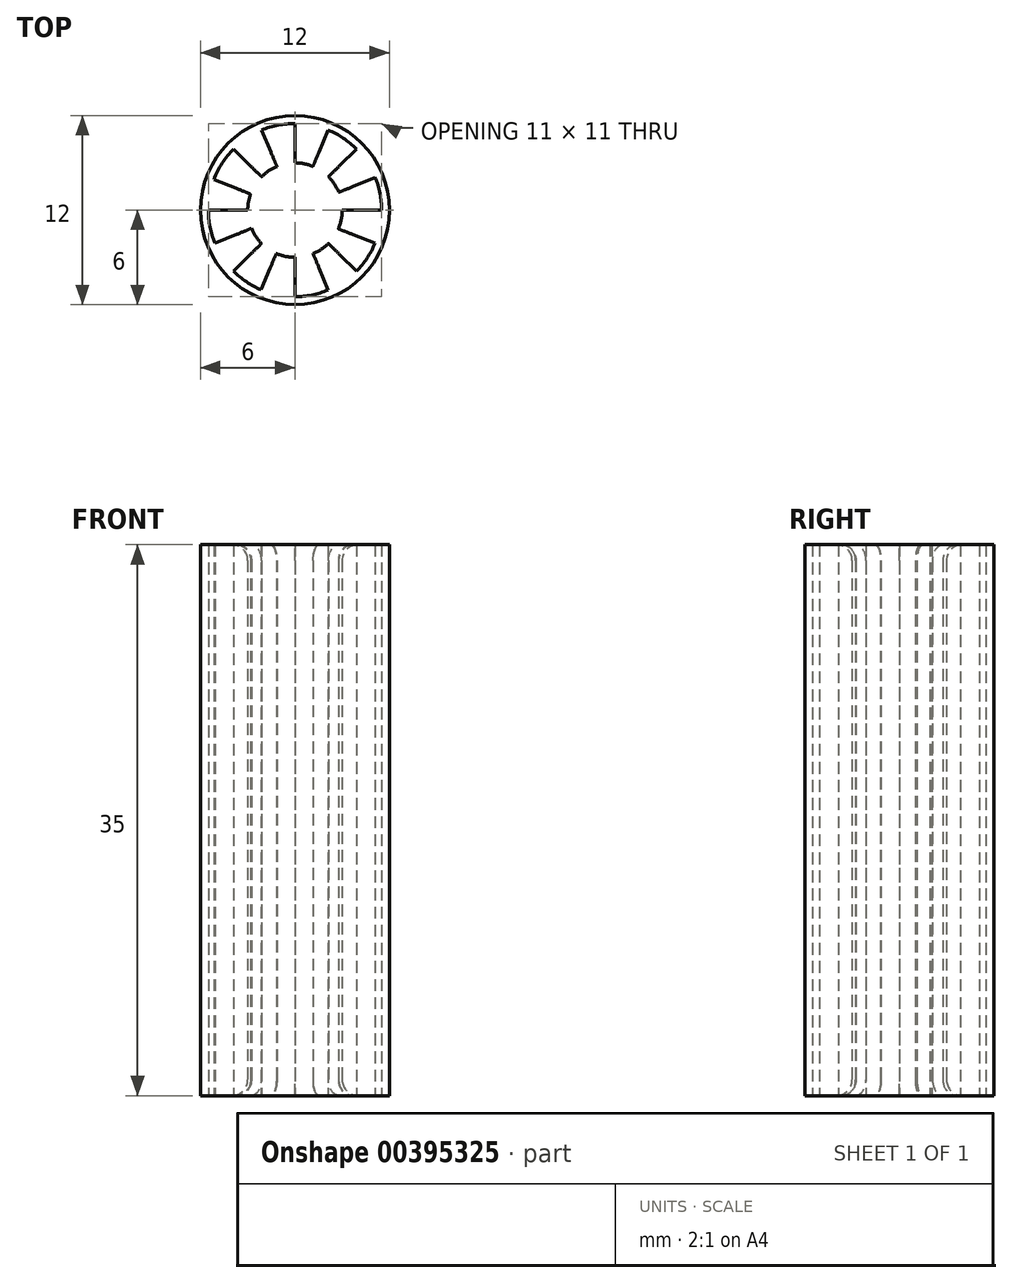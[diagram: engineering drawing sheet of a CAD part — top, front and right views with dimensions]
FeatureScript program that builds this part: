
annotation { "Feature Type Name" : "Feature", "Feature Type Description" : "" }
export const myFeature = defineFeature(function(context is Context, id is Id, definition is map)
    precondition{}
    {
        {
            var Q0;
            Q0=qCreatedBy(makeId("Top.planeOp"),FACE);
            var sketch = newSketch(context, id + "F0", { "sketchPlane" : qUnion([Q0])});
            skCircle(sketch, "E0", {"center": v(0, 0) * mm, "radius": 6 * mm});
            skCircle(sketch, "E1", {"center": v(0, 0) * mm, "radius": 3 * mm});
            skCircle(sketch, "E2", {"center": v(0, 0) * mm, "radius": 5.5 * mm});
            skLineSegment(sketch, "E3", {"start": v(0, 5.5) * mm, "end": v(0, -5.5) * mm});
            skLineSegment(sketch, "E4", {"start": v(-5.5, 0) * mm, "end": v(5.5, 0) * mm});
            skPoint(sketch, "E5", {"position": v(-3.9, 3.88) * mm});
            skPoint(sketch, "E6", {"position": v(3.9, 3.88) * mm});
            skPoint(sketch, "E7", {"position": v(-3.9, -3.88) * mm});
            skPoint(sketch, "E8", {"position": v(3.9, -3.88) * mm});
            skLineSegment(sketch, "E9", {"start": v(-3.9, 3.88) * mm, "end": v(3.9, -3.88) * mm});
            skLineSegment(sketch, "E10", {"start": v(3.9, 3.88) * mm, "end": v(-3.9, -3.88) * mm});
            skPoint(sketch, "E11", {"position": v(-2.1, 5.08) * mm});
            skPoint(sketch, "E12", {"position": v(2.11, -5.08) * mm});
            skPoint(sketch, "E13", {"position": v(5.08, -2.1) * mm});
            skPoint(sketch, "E14", {"position": v(5.1, 2.08) * mm});
            skPoint(sketch, "E15", {"position": v(2.1, 5.08) * mm});
            skPoint(sketch, "E16", {"position": v(-5.15, 1.94) * mm});
            skPoint(sketch, "E17", {"position": v(-5.08, -2.1) * mm});
            skPoint(sketch, "E18", {"position": v(-2.15, -5.06) * mm});
            skLineSegment(sketch, "E19", {"start": v(-2.1, 5.08) * mm, "end": v(2.11, -5.08) * mm});
            skLineSegment(sketch, "E20", {"start": v(5.1, 2.08) * mm, "end": v(-5.08, -2.1) * mm});
            skLineSegment(sketch, "E21", {"start": v(2.11, 5.08) * mm, "end": v(-2.15, -5.06) * mm});
            skLineSegment(sketch, "E22", {"start": v(-5.15, 1.94) * mm, "end": v(5.08, -2.1) * mm});
            skSolve(sketch);
        }
        {
            var Q0;
            Q0=qSketchRegion(id+"F0",true);
            var Q1;
            {var subQ0=sQuery(id+"F0.wireOp",EDGE,"E22");var subQ1=sQuery(id+"F0.wireOp",EDGE,"E1");var subQ2=makeQuery(id+"F0.imprint","INTERSECT",VERTEX,{"disambiguationData":[OD(0.0)],"derivedFrom":[subQ1,subQ0]});Q1=makeQuery(id+"F0.imprint","IMPRINT",FACE,{"disambiguationData":[TD([[makeQuery(id+"F0.imprint","IMPRINT",EDGE,{"disambiguationData":[TD([[subQ2,-1.0]])],"derivedFrom":subQ1}),-1.0]])]});}
            var Q2;
            {var subQ0=sQuery(id+"F0.wireOp",EDGE,"E19");var subQ1=sQuery(id+"F0.wireOp",EDGE,"E1");var subQ2=makeQuery(id+"F0.imprint","INTERSECT",VERTEX,{"disambiguationData":[OD(0.0)],"derivedFrom":[subQ1,subQ0]});Q2=makeQuery(id+"F0.imprint","IMPRINT",FACE,{"disambiguationData":[TD([[makeQuery(id+"F0.imprint","IMPRINT",EDGE,{"disambiguationData":[TD([[subQ2,-1.0]])],"derivedFrom":subQ1}),-1.0]])]});}
            var Q3;
            {var subQ0=sQuery(id+"F0.wireOp",EDGE,"E21");var subQ1=sQuery(id+"F0.wireOp",EDGE,"E1");var subQ2=makeQuery(id+"F0.imprint","INTERSECT",VERTEX,{"disambiguationData":[OD(0.0)],"derivedFrom":[subQ1,subQ0]});Q3=makeQuery(id+"F0.imprint","IMPRINT",FACE,{"disambiguationData":[TD([[makeQuery(id+"F0.imprint","IMPRINT",EDGE,{"disambiguationData":[TD([[subQ2,-1.0]])],"derivedFrom":subQ1}),-1.0]])]});}
            var Q4;
            {var subQ0=sQuery(id+"F0.wireOp",EDGE,"E20");var subQ1=sQuery(id+"F0.wireOp",EDGE,"E1");var subQ2=makeQuery(id+"F0.imprint","INTERSECT",VERTEX,{"disambiguationData":[OD(0.0)],"derivedFrom":[subQ1,subQ0]});Q4=makeQuery(id+"F0.imprint","IMPRINT",FACE,{"disambiguationData":[TD([[makeQuery(id+"F0.imprint","IMPRINT",EDGE,{"disambiguationData":[TD([[subQ2,-1.0]])],"derivedFrom":subQ1}),-1.0]])]});}
            var Q5;
            {var subQ0=sQuery(id+"F0.wireOp",EDGE,"E4");var subQ1=sQuery(id+"F0.wireOp",EDGE,"E1");var subQ2=makeQuery(id+"F0.imprint","INTERSECT",VERTEX,{"disambiguationData":[OD(0.0)],"derivedFrom":[subQ1,subQ0]});Q5=makeQuery(id+"F0.imprint","IMPRINT",FACE,{"disambiguationData":[TD([[makeQuery(id+"F0.imprint","IMPRINT",EDGE,{"disambiguationData":[TD([[subQ2,1.0]])],"derivedFrom":subQ1}),-1.0]])]});}
            var Q6;
            {var subQ0=sQuery(id+"F0.wireOp",EDGE,"E19");var subQ1=sQuery(id+"F0.wireOp",EDGE,"E1");var subQ2=makeQuery(id+"F0.imprint","INTERSECT",VERTEX,{"disambiguationData":[OD(1.0)],"derivedFrom":[subQ1,subQ0]});Q6=makeQuery(id+"F0.imprint","IMPRINT",FACE,{"disambiguationData":[TD([[makeQuery(id+"F0.imprint","IMPRINT",EDGE,{"disambiguationData":[TD([[subQ2,-1.0]])],"derivedFrom":subQ1}),-1.0]])]});}
            var Q7;
            {var subQ0=sQuery(id+"F0.wireOp",EDGE,"E21");var subQ1=sQuery(id+"F0.wireOp",EDGE,"E1");var subQ2=makeQuery(id+"F0.imprint","INTERSECT",VERTEX,{"disambiguationData":[OD(1.0)],"derivedFrom":[subQ1,subQ0]});Q7=makeQuery(id+"F0.imprint","IMPRINT",FACE,{"disambiguationData":[TD([[makeQuery(id+"F0.imprint","IMPRINT",EDGE,{"disambiguationData":[TD([[subQ2,-1.0]])],"derivedFrom":subQ1}),-1.0]])]});}
            var Q8;
            {var subQ0=sQuery(id+"F0.wireOp",EDGE,"E20");var subQ1=sQuery(id+"F0.wireOp",EDGE,"E1");var subQ2=makeQuery(id+"F0.imprint","INTERSECT",VERTEX,{"disambiguationData":[OD(1.0)],"derivedFrom":[subQ1,subQ0]});Q8=makeQuery(id+"F0.imprint","IMPRINT",FACE,{"disambiguationData":[TD([[makeQuery(id+"F0.imprint","IMPRINT",EDGE,{"disambiguationData":[TD([[subQ2,-1.0]])],"derivedFrom":subQ1}),-1.0]])]});}
            extrude(context, id + "F1", {"entities" : qUnion([Q0, Q1, Q2, Q3, Q4, Q5, Q6, Q7, Q8]), "depth" : 35 * mm});
        }
        {
            var Q0;
            {var subQ0=sQuery(id+"F0.wireOp",EDGE,"E1");Q0=makeQuery(id+"F1.opExtrude","CAP_EDGE",EDGE,{"disambiguationData":[OSD([subQ0]),TDD([makeQuery(id+"F0.imprint","IMPRINT",EDGE,{"disambiguationData":[TD([[makeQuery(id+"F0.imprint","INTERSECT",VERTEX,{"disambiguationData":[OD(0.0)],"derivedFrom":[subQ0,sQuery(id+"F0.wireOp",EDGE,"E19")]}),-1.0]])],"derivedFrom":subQ0})])],"isStart":false});}
            var Q1;
            {var subQ0=sQuery(id+"F0.wireOp",EDGE,"E1");Q1=makeQuery(id+"F1.opExtrude","CAP_EDGE",EDGE,{"disambiguationData":[OSD([subQ0]),TDD([makeQuery(id+"F0.imprint","IMPRINT",EDGE,{"disambiguationData":[TD([[makeQuery(id+"F0.imprint","INTERSECT",VERTEX,{"disambiguationData":[OD(0.0)],"derivedFrom":[subQ0,sQuery(id+"F0.wireOp",EDGE,"E21")]}),-1.0]])],"derivedFrom":subQ0})])],"isStart":false});}
            var Q2;
            {var subQ0=sQuery(id+"F0.wireOp",EDGE,"E1");Q2=makeQuery(id+"F1.opExtrude","CAP_EDGE",EDGE,{"disambiguationData":[OSD([subQ0]),TDD([makeQuery(id+"F0.imprint","IMPRINT",EDGE,{"disambiguationData":[TD([[makeQuery(id+"F0.imprint","INTERSECT",VERTEX,{"disambiguationData":[OD(0.0)],"derivedFrom":[subQ0,sQuery(id+"F0.wireOp",EDGE,"E20")]}),-1.0]])],"derivedFrom":subQ0})])],"isStart":false});}
            var Q3;
            {var subQ0=sQuery(id+"F0.wireOp",EDGE,"E1");Q3=makeQuery(id+"F1.opExtrude","CAP_EDGE",EDGE,{"disambiguationData":[OSD([subQ0]),TDD([makeQuery(id+"F0.imprint","IMPRINT",EDGE,{"disambiguationData":[TD([[makeQuery(id+"F0.imprint","INTERSECT",VERTEX,{"disambiguationData":[OD(0.0)],"derivedFrom":[subQ0,sQuery(id+"F0.wireOp",EDGE,"E4")]}),1.0]])],"derivedFrom":subQ0})])],"isStart":false});}
            var Q4;
            {var subQ0=sQuery(id+"F0.wireOp",EDGE,"E1");Q4=makeQuery(id+"F1.opExtrude","CAP_EDGE",EDGE,{"disambiguationData":[OSD([subQ0]),TDD([makeQuery(id+"F0.imprint","IMPRINT",EDGE,{"disambiguationData":[TD([[makeQuery(id+"F0.imprint","INTERSECT",VERTEX,{"disambiguationData":[OD(1.0)],"derivedFrom":[subQ0,sQuery(id+"F0.wireOp",EDGE,"E19")]}),-1.0]])],"derivedFrom":subQ0})])],"isStart":false});}
            var Q5;
            {var subQ0=sQuery(id+"F0.wireOp",EDGE,"E1");Q5=makeQuery(id+"F1.opExtrude","CAP_EDGE",EDGE,{"disambiguationData":[OSD([subQ0]),TDD([makeQuery(id+"F0.imprint","IMPRINT",EDGE,{"disambiguationData":[TD([[makeQuery(id+"F0.imprint","INTERSECT",VERTEX,{"disambiguationData":[OD(1.0)],"derivedFrom":[subQ0,sQuery(id+"F0.wireOp",EDGE,"E21")]}),-1.0]])],"derivedFrom":subQ0})])],"isStart":false});}
            var Q6;
            {var subQ0=sQuery(id+"F0.wireOp",EDGE,"E1");Q6=makeQuery(id+"F1.opExtrude","CAP_EDGE",EDGE,{"disambiguationData":[OSD([subQ0]),TDD([makeQuery(id+"F0.imprint","IMPRINT",EDGE,{"disambiguationData":[TD([[makeQuery(id+"F0.imprint","INTERSECT",VERTEX,{"disambiguationData":[OD(1.0)],"derivedFrom":[subQ0,sQuery(id+"F0.wireOp",EDGE,"E20")]}),-1.0]])],"derivedFrom":subQ0})])],"isStart":false});}
            var Q7;
            {var subQ0=sQuery(id+"F0.wireOp",EDGE,"E1");Q7=makeQuery(id+"F1.opExtrude","CAP_EDGE",EDGE,{"disambiguationData":[OSD([subQ0]),TDD([makeQuery(id+"F0.imprint","IMPRINT",EDGE,{"disambiguationData":[TD([[makeQuery(id+"F0.imprint","INTERSECT",VERTEX,{"disambiguationData":[OD(0.0)],"derivedFrom":[subQ0,sQuery(id+"F0.wireOp",EDGE,"E22")]}),-1.0]])],"derivedFrom":subQ0})])],"isStart":false});}
            var Q8;
            {var subQ0=sQuery(id+"F0.wireOp",EDGE,"E1");Q8=makeQuery(id+"F1.opExtrude","CAP_EDGE",EDGE,{"disambiguationData":[OSD([subQ0]),TDD([makeQuery(id+"F0.imprint","IMPRINT",EDGE,{"disambiguationData":[TD([[makeQuery(id+"F0.imprint","INTERSECT",VERTEX,{"disambiguationData":[OD(1.0)],"derivedFrom":[subQ0,sQuery(id+"F0.wireOp",EDGE,"E20")]}),-1.0]])],"derivedFrom":subQ0})])],"isStart":true});}
            var Q9;
            {var subQ0=sQuery(id+"F0.wireOp",EDGE,"E1");Q9=makeQuery(id+"F1.opExtrude","CAP_EDGE",EDGE,{"disambiguationData":[OSD([subQ0]),TDD([makeQuery(id+"F0.imprint","IMPRINT",EDGE,{"disambiguationData":[TD([[makeQuery(id+"F0.imprint","INTERSECT",VERTEX,{"disambiguationData":[OD(1.0)],"derivedFrom":[subQ0,sQuery(id+"F0.wireOp",EDGE,"E21")]}),-1.0]])],"derivedFrom":subQ0})])],"isStart":true});}
            var Q10;
            {var subQ0=sQuery(id+"F0.wireOp",EDGE,"E1");Q10=makeQuery(id+"F1.opExtrude","CAP_EDGE",EDGE,{"disambiguationData":[OSD([subQ0]),TDD([makeQuery(id+"F0.imprint","IMPRINT",EDGE,{"disambiguationData":[TD([[makeQuery(id+"F0.imprint","INTERSECT",VERTEX,{"disambiguationData":[OD(1.0)],"derivedFrom":[subQ0,sQuery(id+"F0.wireOp",EDGE,"E19")]}),-1.0]])],"derivedFrom":subQ0})])],"isStart":true});}
            var Q11;
            {var subQ0=sQuery(id+"F0.wireOp",EDGE,"E1");Q11=makeQuery(id+"F1.opExtrude","CAP_EDGE",EDGE,{"disambiguationData":[OSD([subQ0]),TDD([makeQuery(id+"F0.imprint","IMPRINT",EDGE,{"disambiguationData":[TD([[makeQuery(id+"F0.imprint","INTERSECT",VERTEX,{"disambiguationData":[OD(0.0)],"derivedFrom":[subQ0,sQuery(id+"F0.wireOp",EDGE,"E4")]}),1.0]])],"derivedFrom":subQ0})])],"isStart":true});}
            var Q12;
            {var subQ0=sQuery(id+"F0.wireOp",EDGE,"E1");Q12=makeQuery(id+"F1.opExtrude","CAP_EDGE",EDGE,{"disambiguationData":[OSD([subQ0]),TDD([makeQuery(id+"F0.imprint","IMPRINT",EDGE,{"disambiguationData":[TD([[makeQuery(id+"F0.imprint","INTERSECT",VERTEX,{"disambiguationData":[OD(0.0)],"derivedFrom":[subQ0,sQuery(id+"F0.wireOp",EDGE,"E20")]}),-1.0]])],"derivedFrom":subQ0})])],"isStart":true});}
            var Q13;
            {var subQ0=sQuery(id+"F0.wireOp",EDGE,"E1");Q13=makeQuery(id+"F1.opExtrude","CAP_EDGE",EDGE,{"disambiguationData":[OSD([subQ0]),TDD([makeQuery(id+"F0.imprint","IMPRINT",EDGE,{"disambiguationData":[TD([[makeQuery(id+"F0.imprint","INTERSECT",VERTEX,{"disambiguationData":[OD(0.0)],"derivedFrom":[subQ0,sQuery(id+"F0.wireOp",EDGE,"E21")]}),-1.0]])],"derivedFrom":subQ0})])],"isStart":true});}
            var Q14;
            {var subQ0=sQuery(id+"F0.wireOp",EDGE,"E1");Q14=makeQuery(id+"F1.opExtrude","CAP_EDGE",EDGE,{"disambiguationData":[OSD([subQ0]),TDD([makeQuery(id+"F0.imprint","IMPRINT",EDGE,{"disambiguationData":[TD([[makeQuery(id+"F0.imprint","INTERSECT",VERTEX,{"disambiguationData":[OD(0.0)],"derivedFrom":[subQ0,sQuery(id+"F0.wireOp",EDGE,"E19")]}),-1.0]])],"derivedFrom":subQ0})])],"isStart":true});}
            var Q15;
            {var subQ0=sQuery(id+"F0.wireOp",EDGE,"E1");Q15=makeQuery(id+"F1.opExtrude","CAP_EDGE",EDGE,{"disambiguationData":[OSD([subQ0]),TDD([makeQuery(id+"F0.imprint","IMPRINT",EDGE,{"disambiguationData":[TD([[makeQuery(id+"F0.imprint","INTERSECT",VERTEX,{"disambiguationData":[OD(0.0)],"derivedFrom":[subQ0,sQuery(id+"F0.wireOp",EDGE,"E22")]}),-1.0]])],"derivedFrom":subQ0})])],"isStart":true});}
            fillet(context, id + "F2", {"entities" : qUnion([Q0, Q1, Q2, Q3, Q4, Q5, Q6, Q7, Q8, Q9, Q10, Q11, Q12, Q13, Q14, Q15]), "radius" : 1 * mm, "tangentPropagation" : true, "allowEdgeOverflow" : false});
        }
    });
